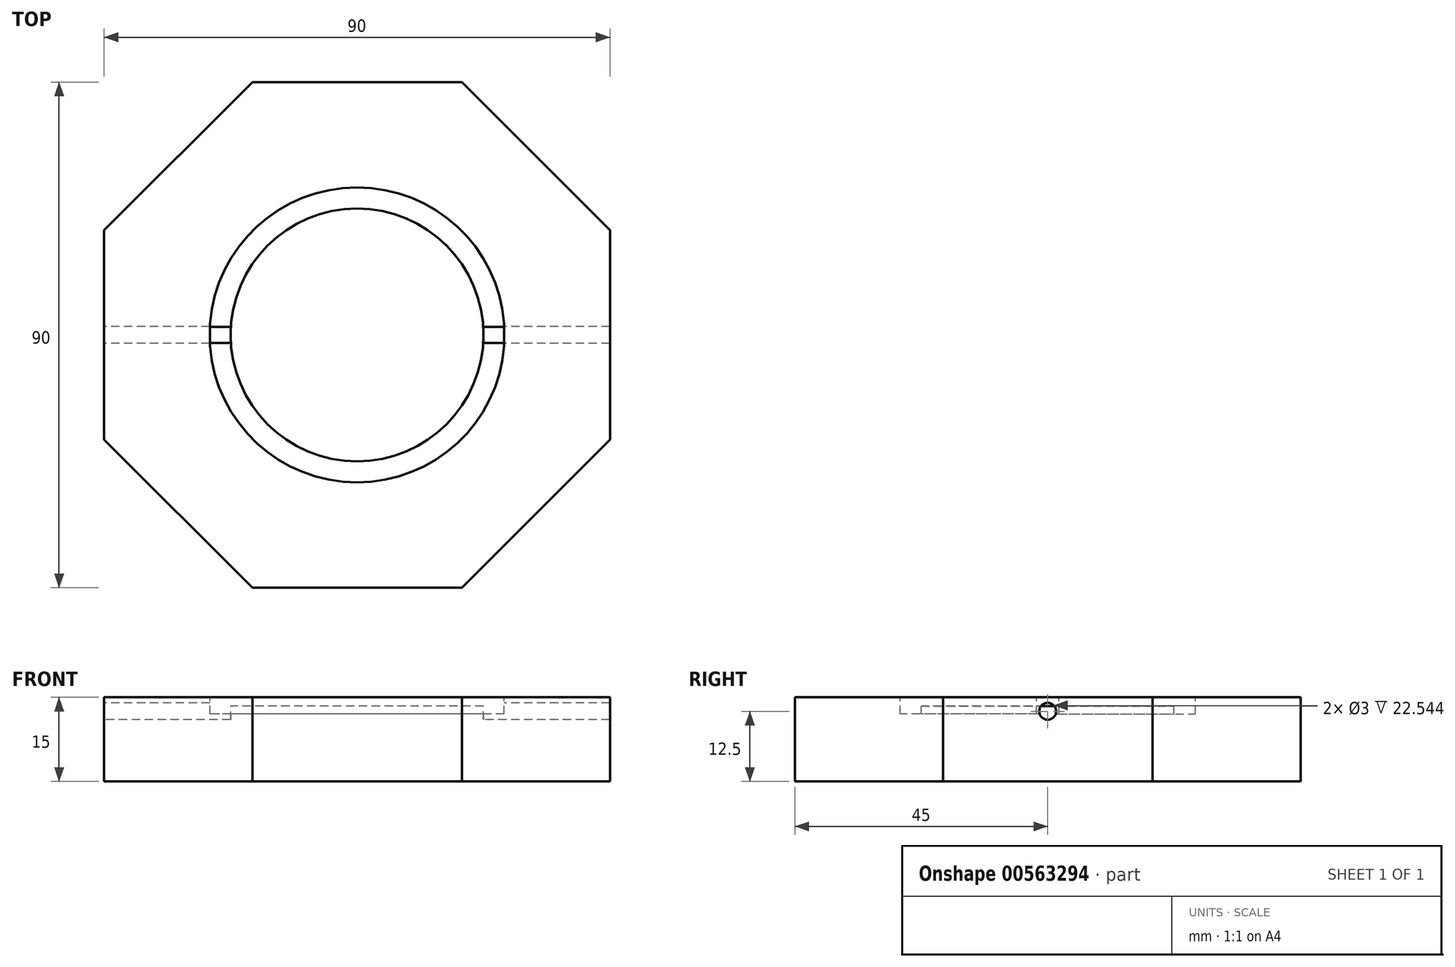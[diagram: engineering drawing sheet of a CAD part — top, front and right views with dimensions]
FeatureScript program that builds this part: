
annotation { "Feature Type Name" : "Feature", "Feature Type Description" : "" }
export const myFeature = defineFeature(function(context is Context, id is Id, definition is map)
    precondition{}
    {
        {
            var Q0;
            Q0=qCreatedBy(makeId("Top.planeOp"),FACE);
            var sketch = newSketch(context, id + "F0", { "sketchPlane" : qUnion([Q0])});
            skCircle(sketch, "E0.cCircle", {"center": v(0, 0) * mm, "radius": 45 * mm, "construction": true});
            skLineSegment(sketch, "E0.0", {"start": v(-18.64, 45) * mm, "end": v(18.64, 45) * mm});
            skLineSegment(sketch, "E0.1", {"start": v(18.64, 45) * mm, "end": v(45, 18.64) * mm});
            skLineSegment(sketch, "E0.2", {"start": v(45, 18.64) * mm, "end": v(45, -18.64) * mm});
            skLineSegment(sketch, "E0.3", {"start": v(45, -18.64) * mm, "end": v(18.64, -45) * mm});
            skLineSegment(sketch, "E0.4", {"start": v(18.64, -45) * mm, "end": v(-18.64, -45) * mm});
            skLineSegment(sketch, "E0.5", {"start": v(-18.64, -45) * mm, "end": v(-45, -18.64) * mm});
            skLineSegment(sketch, "E0.6", {"start": v(-45, -18.64) * mm, "end": v(-45, 18.64) * mm});
            skLineSegment(sketch, "E0.7", {"start": v(-45, 18.64) * mm, "end": v(-18.64, 45) * mm});
            skPoint(sketch, "E0.0.midPoint", {"position": v(0, 45) * mm});
            skSolve(sketch);
        }
        {
            var Q0;
            Q0=makeQuery(id+"F0.imprint","IMPRINT",FACE,{"disambiguationData":[TD([[makeQuery(id+"F0.imprint","IMPRINT",EDGE,{"derivedFrom":sQuery(id+"F0.wireOp",EDGE,"E0.0")}),-1.0]])]});
            extrude(context, id + "F1", {"entities" : qUnion([Q0]), "depth" : 40 * mm, "offsetDistance" : 25 * mm});
        }
        {
            var Q0;
            Q0=makeQuery(id+"F1.opExtrude","CAP_FACE",FACE,{"disambiguationData":[OSD([sQuery(id+"F0.wireOp",EDGE,"E0.0"),sQuery(id+"F0.wireOp",EDGE,"E0.1"),sQuery(id+"F0.wireOp",EDGE,"E0.2"),sQuery(id+"F0.wireOp",EDGE,"E0.3"),sQuery(id+"F0.wireOp",EDGE,"E0.4"),sQuery(id+"F0.wireOp",EDGE,"E0.5"),sQuery(id+"F0.wireOp",EDGE,"E0.6"),sQuery(id+"F0.wireOp",EDGE,"E0.7")])],"isStart":false});
            var sketch = newSketch(context, id + "F2", { "sketchPlane" : qUnion([Q0])});
            skArc(sketch, "E1", {"start": v(-26.17, -2) * mm, "mid": v(0, -26.25) * mm, "end": v(26.17, -2) * mm});
            skCircle(sketch, "E2", {"center": v(0, 0) * mm, "radius": 22.5 * mm});
            skArc(sketch, "E3.trimOffspring", {"start": v(26.17, 2) * mm, "mid": v(0, 26.25) * mm, "end": v(-26.17, 2) * mm});
            skLineSegment(sketch, "E4", {"start": v(-26.17, 2) * mm, "end": v(-26.17, -2) * mm});
            skLineSegment(sketch, "E5", {"start": v(26.17, 2) * mm, "end": v(26.17, -2) * mm});
            skSolve(sketch);
        }
        {
            var Q0;
            Q0=makeQuery(id+"F2.imprint","IMPRINT",FACE,{"disambiguationData":[TD([[makeQuery(id+"F2.imprint","IMPRINT",EDGE,{"derivedFrom":sQuery(id+"F2.wireOp",EDGE,"E1")}),1.0]])]});
            extrude(context, id + "F3", {"entities" : qUnion([Q0]), "operationType" : NewBodyOperationType.REMOVE, "oppositeDirection" : true, "depth" : 3 * mm, "offsetDistance" : 25 * mm});
        }
        {
            var Q0;
            Q0=makeQuery(id+"F0.imprint","IMPRINT",FACE,{"disambiguationData":[TD([[makeQuery(id+"F0.imprint","IMPRINT",EDGE,{"derivedFrom":sQuery(id+"F0.wireOp",EDGE,"E0.0")}),-1.0]])]});
            var sketch = newSketch(context, id + "F4", { "sketchPlane" : qUnion([Q0])});
            skCircle(sketch, "E6.cCircle", {"center": v(0, 0) * mm, "radius": 45 * mm, "construction": true});
            skLineSegment(sketch, "E6.0", {"start": v(18.64, -45) * mm, "end": v(-18.64, -45) * mm});
            skLineSegment(sketch, "E6.1", {"start": v(-18.64, -45) * mm, "end": v(-45, -18.64) * mm});
            skLineSegment(sketch, "E6.2", {"start": v(-45, -18.64) * mm, "end": v(-45, 18.64) * mm});
            skLineSegment(sketch, "E6.3", {"start": v(-45, 18.64) * mm, "end": v(-18.64, 45) * mm});
            skLineSegment(sketch, "E6.4", {"start": v(-18.64, 45) * mm, "end": v(18.64, 45) * mm});
            skLineSegment(sketch, "E6.5", {"start": v(18.64, 45) * mm, "end": v(45, 18.64) * mm});
            skLineSegment(sketch, "E6.6", {"start": v(45, 18.64) * mm, "end": v(45, -18.64) * mm});
            skLineSegment(sketch, "E6.7", {"start": v(45, -18.64) * mm, "end": v(18.64, -45) * mm});
            skPoint(sketch, "E6.0.midPoint", {"position": v(0, -45) * mm});
            skSolve(sketch);
        }
        {
            var Q0;
            Q0=makeQuery(id+"F4.imprint","IMPRINT",FACE,{"disambiguationData":[TD([[makeQuery(id+"F4.imprint","IMPRINT",EDGE,{"derivedFrom":sQuery(id+"F4.wireOp",EDGE,"E6.0")}),-1.0]])]});
            extrude(context, id + "F5", {"entities" : qUnion([Q0]), "operationType" : NewBodyOperationType.ADD, "depth" : 25 * mm, "offsetDistance" : 25 * mm});
        }
        {
            var Q0;
            Q0=makeQuery(id+"F0.imprint","IMPRINT",FACE,{"disambiguationData":[TD([[makeQuery(id+"F0.imprint","IMPRINT",EDGE,{"derivedFrom":sQuery(id+"F0.wireOp",EDGE,"E0.0")}),-1.0]])]});
            extrude(context, id + "F6", {"entities" : qUnion([Q0]), "operationType" : NewBodyOperationType.ADD, "depth" : 25 * mm, "offsetDistance" : 25 * mm});
        }
        {
            var Q0;
            Q0=makeQuery(id+"F0.imprint","IMPRINT",FACE,{"disambiguationData":[TD([[makeQuery(id+"F0.imprint","IMPRINT",EDGE,{"derivedFrom":sQuery(id+"F0.wireOp",EDGE,"E0.0")}),-1.0]])]});
            extrude(context, id + "F7", {"entities" : qUnion([Q0]), "operationType" : NewBodyOperationType.REMOVE, "depth" : 25 * mm, "offsetDistance" : 25 * mm});
        }
        {
            var Q0;
            Q0=qCreatedBy(makeId("Right.planeOp"),FACE);
            var sketch = newSketch(context, id + "F8", { "sketchPlane" : qUnion([Q0])});
            skCircle(sketch, "E7", {"center": v(0, 37.5) * mm, "radius": 1.5 * mm});
            skSolve(sketch);
        }
        {
            var Q0;
            Q0 = qSketchRegion(id + "F8", true);
            extrude(context, id + "F9", {"entities" : qUnion([Q0]), "operationType" : NewBodyOperationType.REMOVE, "endBound" : BoundingType.SYMMETRIC, "depth" : 220 * mm, "offsetDistance" : 25 * mm});
        }
        {
            var Q0;
            Q0 = qSketchRegion(id + "F8", true);
            var Q1;
            Q1=makeQuery(id+"F3.boolean.opBoolean","COPY",FACE,{"derivedFrom":makeQuery(id+"F3.opExtrude","SWEPT_FACE",FACE,{"disambiguationData":[OSD([sQuery(id+"F2.wireOp",EDGE,"E2")])]})});
            extrude(context, id + "F10", {"entities" : qUnion([Q0]), "operationType" : NewBodyOperationType.ADD, "endBound" : BoundingType.UP_TO_SURFACE, "depth" : 25 * mm, "endBoundEntityFace" : qUnion([Q1]), "offsetDistance" : 25 * mm});
        }
        {
            var Q0;
            Q0 = qSketchRegion(id + "F8", true);
            var Q1;
            {var subQ0=sQuery(id+"F2.wireOp",EDGE,"E2");Q1=makeQuery(id+"F10.boolean.opBoolean","MERGE",FACE,{"derivedFrom":[makeQuery(id+"F3.boolean.opBoolean","COPY",FACE,{"derivedFrom":makeQuery(id+"F3.opExtrude","SWEPT_FACE",FACE,{"disambiguationData":[OSD([subQ0])]})}),makeQuery(id+"F10.opExtrude","CAP_FACE",FACE,{"disambiguationData":[OSD([subQ0])],"isStart":false})]});}
            extrude(context, id + "F11", {"entities" : qUnion([Q0]), "operationType" : NewBodyOperationType.ADD, "endBound" : BoundingType.UP_TO_SURFACE, "oppositeDirection" : true, "depth" : 25 * mm, "endBoundEntityFace" : qUnion([Q1]), "offsetDistance" : 25 * mm});
        }
        {
            var Q0;
            Q0=makeQuery(id+"F3.boolean.opBoolean","SPLIT",FACE,{"disambiguationData":[TD([makeQuery(id+"F3.opExtrude","SWEPT_FACE",FACE,{"disambiguationData":[OSD([sQuery(id+"F2.wireOp",EDGE,"E2")])]})])],"derivedFrom":makeQuery(id+"F1.opExtrude","CAP_FACE",FACE,{"disambiguationData":[OSD([sQuery(id+"F0.wireOp",EDGE,"E0.0"),sQuery(id+"F0.wireOp",EDGE,"E0.1"),sQuery(id+"F0.wireOp",EDGE,"E0.2"),sQuery(id+"F0.wireOp",EDGE,"E0.3"),sQuery(id+"F0.wireOp",EDGE,"E0.4"),sQuery(id+"F0.wireOp",EDGE,"E0.5"),sQuery(id+"F0.wireOp",EDGE,"E0.6"),sQuery(id+"F0.wireOp",EDGE,"E0.7")])],"isStart":false})});
            extrude(context, id + "F12", {"entities" : qUnion([Q0]), "operationType" : NewBodyOperationType.REMOVE, "oppositeDirection" : true, "depth" : 1.6 * mm, "offsetDistance" : 25 * mm});
        }
    });
